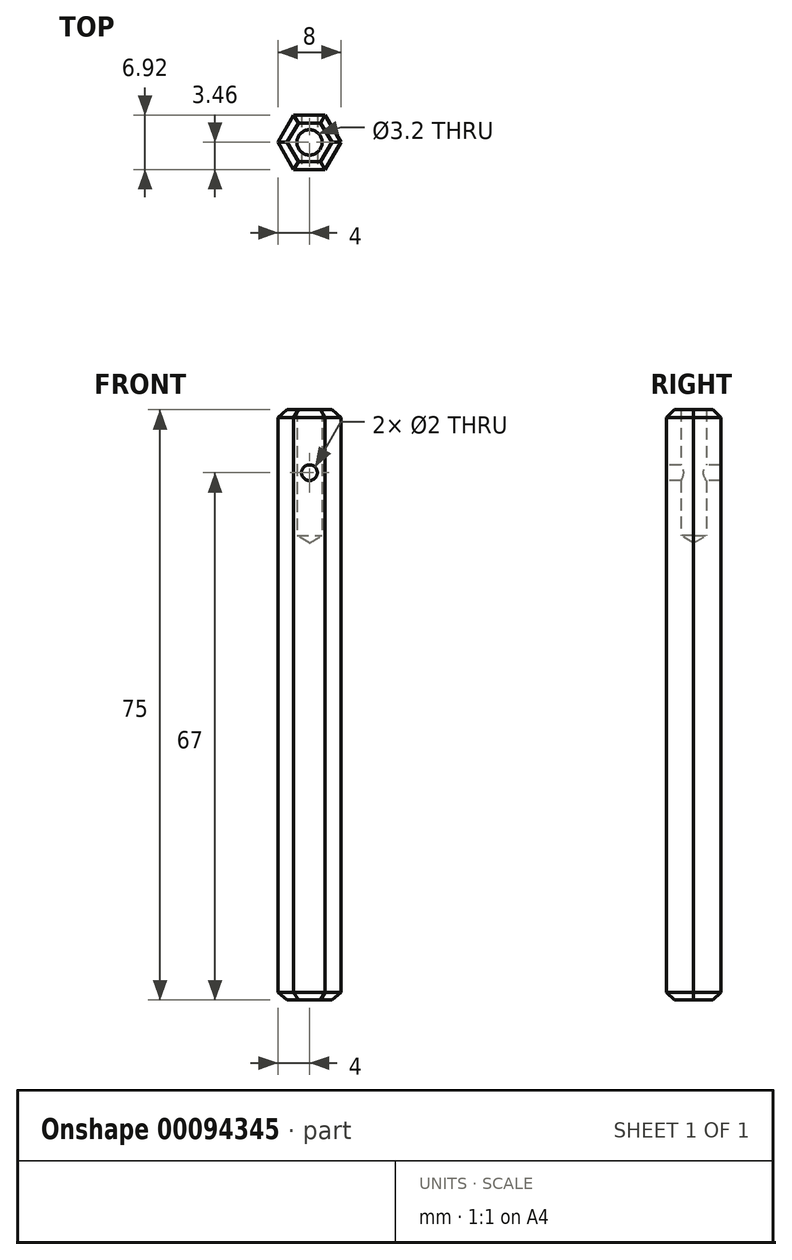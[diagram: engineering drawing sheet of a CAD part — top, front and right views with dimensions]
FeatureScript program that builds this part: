
annotation { "Feature Type Name" : "Feature", "Feature Type Description" : "" }
export const myFeature = defineFeature(function(context is Context, id is Id, definition is map)
    precondition{}
    {
        {
            var Q0;
            Q0=qCreatedBy(makeId("Top.planeOp"),FACE);
            var sketch = newSketch(context, id + "F0", { "sketchPlane" : qUnion([Q0])});
            skCircle(sketch, "E0.cCircle", {"center": v(0, 0) * mm, "radius": 4 * mm, "construction": true});
            skLineSegment(sketch, "E0.0", {"start": v(2, -3.46) * mm, "end": v(-2, -3.46) * mm});
            skLineSegment(sketch, "E0.1", {"start": v(-2, -3.46) * mm, "end": v(-4, 0) * mm});
            skLineSegment(sketch, "E0.2", {"start": v(-4, 0) * mm, "end": v(-2, 3.46) * mm});
            skLineSegment(sketch, "E0.3", {"start": v(-2, 3.46) * mm, "end": v(2, 3.46) * mm});
            skLineSegment(sketch, "E0.4", {"start": v(2, 3.46) * mm, "end": v(4, 0) * mm});
            skLineSegment(sketch, "E0.5", {"start": v(4, 0) * mm, "end": v(2, -3.46) * mm});
            skSolve(sketch);
        }
        {
            var Q0;
            Q0=makeQuery(id+"F0.imprint","IMPRINT",FACE,{"disambiguationData":[TD([[makeQuery(id+"F0.imprint","IMPRINT",EDGE,{"derivedFrom":sQuery(id+"F0.wireOp",EDGE,"E0.0")}),-1.0]])]});
            extrude(context, id + "F1", {"entities" : qUnion([Q0]), "depth" : 75 * mm});
        }
        {
            var Q0;
            Q0=makeQuery(id+"F1.opExtrude","CAP_FACE",FACE,{"disambiguationData":[OSD([sQuery(id+"F0.wireOp",EDGE,"E0.0"),sQuery(id+"F0.wireOp",EDGE,"E0.1"),sQuery(id+"F0.wireOp",EDGE,"E0.2"),sQuery(id+"F0.wireOp",EDGE,"E0.3"),sQuery(id+"F0.wireOp",EDGE,"E0.4"),sQuery(id+"F0.wireOp",EDGE,"E0.5")])],"isStart":false});
            var sketch = newSketch(context, id + "F2", { "sketchPlane" : qUnion([Q0])});
            skPoint(sketch, "E1", {"position": v(0, 0) * mm});
            skSolve(sketch);
        }
        {
            var Q0;
            Q0=sQuery(id+"F2.wireOp",VERTEX,"E1");
            var Q1;
            Q1=makeQuery(id+"F1.opExtrude","SWEPT_BODY",BODY,{"disambiguationData":[OSD([sQuery(id+"F0.wireOp",EDGE,"E0.0"),sQuery(id+"F0.wireOp",EDGE,"E0.1"),sQuery(id+"F0.wireOp",EDGE,"E0.2"),sQuery(id+"F0.wireOp",EDGE,"E0.3"),sQuery(id+"F0.wireOp",EDGE,"E0.4"),sQuery(id+"F0.wireOp",EDGE,"E0.5")])]});
            hole(context, id + "F3", {"style" : HoleStyle.SIMPLE, "endStyle" : HoleEndStyle.BLIND, "holeDiameter" : 3.2 * mm, "holeDepth" : 16 * mm, "locations" : qUnion([Q0]), "scope" : qUnion([Q1]), "startStyle" : HoleStartStyle.SKETCH});
        }
        {
            var Q0;
            Q0=makeQuery(id+"F1.opExtrude","SWEPT_FACE",FACE,{"disambiguationData":[OSD([sQuery(id+"F0.wireOp",EDGE,"E0.3")])]});
            var sketch = newSketch(context, id + "F4", { "sketchPlane" : qUnion([Q0])});
            skPoint(sketch, "E2", {"position": v(0, 67) * mm});
            skPoint(sketch, "E2.positionSnap0", {"position": v(0, 75) * mm});
            skSolve(sketch);
        }
        {
            var Q0;
            Q0=sQuery(id+"F4.wireOp",VERTEX,"E2");
            var Q1;
            Q1=makeQuery(id+"F1.opExtrude","SWEPT_BODY",BODY,{"disambiguationData":[OSD([sQuery(id+"F0.wireOp",EDGE,"E0.0"),sQuery(id+"F0.wireOp",EDGE,"E0.1"),sQuery(id+"F0.wireOp",EDGE,"E0.2"),sQuery(id+"F0.wireOp",EDGE,"E0.3"),sQuery(id+"F0.wireOp",EDGE,"E0.4"),sQuery(id+"F0.wireOp",EDGE,"E0.5")])]});
            hole(context, id + "F5", {"style" : HoleStyle.SIMPLE, "endStyle" : HoleEndStyle.BLIND, "holeDiameter" : 2 * mm, "holeDepth" : 20 * mm, "locations" : qUnion([Q0]), "scope" : qUnion([Q1]), "startStyle" : HoleStartStyle.SKETCH});
        }
        {
            var Q0;
            Q0=makeQuery(id+"F1.opExtrude","CAP_EDGE",EDGE,{"disambiguationData":[OSD([sQuery(id+"F0.wireOp",EDGE,"E0.3")])],"isStart":false});
            var Q1;
            Q1=makeQuery(id+"F1.opExtrude","CAP_EDGE",EDGE,{"disambiguationData":[OSD([sQuery(id+"F0.wireOp",EDGE,"E0.2")])],"isStart":false});
            var Q2;
            Q2=makeQuery(id+"F1.opExtrude","CAP_EDGE",EDGE,{"disambiguationData":[OSD([sQuery(id+"F0.wireOp",EDGE,"E0.1")])],"isStart":false});
            var Q3;
            Q3=makeQuery(id+"F1.opExtrude","CAP_EDGE",EDGE,{"disambiguationData":[OSD([sQuery(id+"F0.wireOp",EDGE,"E0.0")])],"isStart":false});
            var Q4;
            Q4=makeQuery(id+"F1.opExtrude","CAP_EDGE",EDGE,{"disambiguationData":[OSD([sQuery(id+"F0.wireOp",EDGE,"E0.5")])],"isStart":false});
            var Q5;
            Q5=makeQuery(id+"F1.opExtrude","CAP_EDGE",EDGE,{"disambiguationData":[OSD([sQuery(id+"F0.wireOp",EDGE,"E0.4")])],"isStart":false});
            var Q6;
            Q6=makeQuery(id+"F1.opExtrude","CAP_EDGE",EDGE,{"disambiguationData":[OSD([sQuery(id+"F0.wireOp",EDGE,"E0.2")])],"isStart":true});
            var Q7;
            Q7=makeQuery(id+"F1.opExtrude","CAP_EDGE",EDGE,{"disambiguationData":[OSD([sQuery(id+"F0.wireOp",EDGE,"E0.3")])],"isStart":true});
            var Q8;
            Q8=makeQuery(id+"F1.opExtrude","CAP_EDGE",EDGE,{"disambiguationData":[OSD([sQuery(id+"F0.wireOp",EDGE,"E0.1")])],"isStart":true});
            var Q9;
            Q9=makeQuery(id+"F1.opExtrude","CAP_EDGE",EDGE,{"disambiguationData":[OSD([sQuery(id+"F0.wireOp",EDGE,"E0.0")])],"isStart":true});
            var Q10;
            Q10=makeQuery(id+"F1.opExtrude","CAP_EDGE",EDGE,{"disambiguationData":[OSD([sQuery(id+"F0.wireOp",EDGE,"E0.5")])],"isStart":true});
            var Q11;
            Q11=makeQuery(id+"F1.opExtrude","CAP_EDGE",EDGE,{"disambiguationData":[OSD([sQuery(id+"F0.wireOp",EDGE,"E0.4")])],"isStart":true});
            chamfer(context, id + "F6", {"entities" : qUnion([Q0, Q1, Q2, Q3, Q4, Q5, Q6, Q7, Q8, Q9, Q10, Q11]), "width" : 1 * mm, "tangentPropagation" : true});
        }
    });
